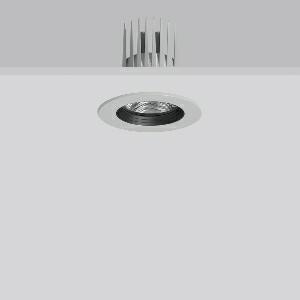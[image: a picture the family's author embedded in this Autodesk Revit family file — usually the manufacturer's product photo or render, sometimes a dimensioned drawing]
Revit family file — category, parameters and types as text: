
# Revit family: heledon_mini_e_901748_004_1_76_fafb
name_source: partatom
category: Lighting Fixtures
units: mm (PartAtom-declared; Revit-internal decimal feet)

## family parameters
Cut with Voids When Loaded = No
Host = Face
Light Source = No
Part Type = Normal
Room Calculation Point = No
Round Connector Dimension = Use Diameter
Shared = No

## types (1)
- HELEDON mini E (1 x LED Modul 940, 3800 lm, 4000)
    Apparent Load = 29 VA
    Approval mark = CE
    CIE Flux Codes = 100 100 100 100 100
    Color Rendering = 92
    Color Temperature = 4000
    Default Elevation = 1800 mm
    Description = Series: HELEDON mini
Round recessed downlight. Housing: die-cast aluminium, powder-coated. Black plastic ring and recessed LED to prevent glare from the side. Optical assembly with reflector made of MIRO-Silver with 98% total light reflection for outstanding efficiency - can be changed without tools. Best colour rendering index Ra>90. Suitable for Recessed ceiling mounting. Installation without tools thanks to spring fastening system. Including separate LED converter with connecting cable 600 mm.High quality converter without flickering and stroboscopic effect. Through-wiring box (5 pole) available as accessory. The following accessories can be mounted without use of tools: interchangeable lenses, decorative glasses, honeycomb louvre, clear and frosted diffusers, white interchangeable plastic ring. 
Colour: silver
Diameter: 124 mm
Height: 3 mm
Cut-out diameter: 114 mm
Recess height: 170 mm
Luminaire: recess height: 120 mm
Lamp: LED
Socket: without socket
Colour temperature: 4000K
Colour rendering index (CRI): 92
System power: 29 W
Rated luminous flux: 3800 lm
Luminous efficiency: 131 lm/W
Control gear: Converter, dimmable, DALI
Protection class: II
Type of protection: IP 20
    Height = 0 mm  [stored 0 ft]
    Lamp = 1 x LED Modul 940
    Lamp Light Flux = 3800 lm
    Lamp count = 1
    Length = 124 mm  [stored 0.406824 ft]
    Lifetime = 50000 h
    Luminous efficacy = 131 lm/W
    Manufacturer = RZB
    ModVariant = No
    Model = 901748.004.1.76
    Mounting Place = Ceiling
    Mounting Type = Recessed
    Number of Poles = 1
    OnlyDefault = Yes
    Power Factor = 1
    Product Name = HELEDON mini E
    Product group = Recessed downlights
    ProductGroupID = 402
    Protection Class = Protection class II
    Protection Degree = IP 20
    RLX_Detail_Level = 1
    RLX_Emergency_Light_Flux = 0 lm
    RLX_Emergency_Type = 0
    RLX_Emergency_Type_DB = No
    RlxData = <blob elided: 127121 chars, md5=88eb559c>
    Socket = socket
    Standby Power = 0 W
    System Light Flux = 3800 lm
    System Power = 29 W
    Type Comments = Product without accessories
    Type Image = 901657.004.jpg
    URL = http://relux.com
    VarID = ---
    Voltage = 230 V
    Voltage Range = 220-240 V
    Weight = 0.00 kg
    Width = 0 mm  [stored 0 ft]

note: [stored X ft] marks values corroborated as IEEE doubles in the binary element streams (Revit-internal decimal feet)

## geometry (parser evidence)
native form markers: Blend x4, Sweep x12
no freeform markers — native parametric forms only
